annotation { "Feature Type Name" : "Feature", "Feature Type Description" : "" }
export const myFeature = defineFeature(function(context is Context, id is Id, definition is map)
    precondition{}
    {
        {
            var Q0;
            Q0=qCreatedBy(makeId("Front.planeOp"),FACE);
            var sketch = newSketch(context, id + "F0", { "sketchPlane" : qUnion([Q0])});
            skText(sketch, "E0", { "text": "Maya\'s Gymnastic Medals", "fontName": "OpenSans-Bold.ttf"});
            const initialGuessF0  = {"E0": [-0.0474, 0.00076, 1, 0, 0.0053]};
            skSetInitialGuess(sketch, initialGuessF0);
            skSolve(sketch);
        }
        {
            var Q0;
            Q0 = qSketchRegion(id + "F0", true);
            extrude(context, id + "F1", {"entities" : qUnion([Q0]), "depth" : 3 * mm, "offsetDistance" : 25 * mm});
        }
        {
            var Q0;
            Q0=makeQuery(id+"F1.opExtrude","SWEPT_BODY",BODY,{"disambiguationData":[OSD([sQuery(id+"F0.wireOp",EDGE,"E0.sketch_text.stroke-44"),sQuery(id+"F0.wireOp",EDGE,"E0.sketch_text.stroke-45"),sQuery(id+"F0.wireOp",EDGE,"E0.sketch_text.stroke-46"),sQuery(id+"F0.wireOp",EDGE,"E0.sketch_text.stroke-47"),sQuery(id+"F0.wireOp",EDGE,"E0.sketch_text.stroke-48"),sQuery(id+"F0.wireOp",EDGE,"E0.sketch_text.stroke-49"),sQuery(id+"F0.wireOp",EDGE,"E0.sketch_text.stroke-50"),sQuery(id+"F0.wireOp",EDGE,"E0.sketch_text.stroke-51"),sQuery(id+"F0.wireOp",EDGE,"E0.sketch_text.stroke-52"),sQuery(id+"F0.wireOp",EDGE,"E0.sketch_text.stroke-53"),sQuery(id+"F0.wireOp",EDGE,"E0.sketch_text.stroke-54"),sQuery(id+"F0.wireOp",EDGE,"E0.sketch_text.stroke-55"),sQuery(id+"F0.wireOp",EDGE,"E0.sketch_text.stroke-56"),sQuery(id+"F0.wireOp",EDGE,"E0.sketch_text.stroke-57"),sQuery(id+"F0.wireOp",EDGE,"E0.sketch_text.stroke-58"),sQuery(id+"F0.wireOp",EDGE,"E0.sketch_text.stroke-59"),sQuery(id+"F0.wireOp",EDGE,"E0.sketch_text.stroke-60")])]});
            var Q1;
            Q1=makeQuery(id+"F1.opExtrude","SWEPT_BODY",BODY,{"disambiguationData":[OSD([sQuery(id+"F0.wireOp",EDGE,"E0.sketch_text.stroke-135"),sQuery(id+"F0.wireOp",EDGE,"E0.sketch_text.stroke-136"),sQuery(id+"F0.wireOp",EDGE,"E0.sketch_text.stroke-137"),sQuery(id+"F0.wireOp",EDGE,"E0.sketch_text.stroke-138"),sQuery(id+"F0.wireOp",EDGE,"E0.sketch_text.stroke-139"),sQuery(id+"F0.wireOp",EDGE,"E0.sketch_text.stroke-140"),sQuery(id+"F0.wireOp",EDGE,"E0.sketch_text.stroke-141"),sQuery(id+"F0.wireOp",EDGE,"E0.sketch_text.stroke-142"),sQuery(id+"F0.wireOp",EDGE,"E0.sketch_text.stroke-143"),sQuery(id+"F0.wireOp",EDGE,"E0.sketch_text.stroke-144"),sQuery(id+"F0.wireOp",EDGE,"E0.sketch_text.stroke-145"),sQuery(id+"F0.wireOp",EDGE,"E0.sketch_text.stroke-146"),sQuery(id+"F0.wireOp",EDGE,"E0.sketch_text.stroke-147"),sQuery(id+"F0.wireOp",EDGE,"E0.sketch_text.stroke-148"),sQuery(id+"F0.wireOp",EDGE,"E0.sketch_text.stroke-149"),sQuery(id+"F0.wireOp",EDGE,"E0.sketch_text.stroke-150"),sQuery(id+"F0.wireOp",EDGE,"E0.sketch_text.stroke-151")])]});
            transform(context, id + "F2", {"entities" : qUnion([Q0, Q1]), "transformType" : TransformType.TRANSLATION_3D, "dx" : 0 * mm, "dy" : 0 * mm, "dz" : 1.5 * mm, "makeCopy" : false});
        }
        {
            var Q0;
            Q0=makeQuery(id+"F1.opExtrude","SWEPT_BODY",BODY,{"disambiguationData":[OSD([sQuery(id+"F0.wireOp",EDGE,"E0.sketch_text.stroke-86"),sQuery(id+"F0.wireOp",EDGE,"E0.sketch_text.stroke-87"),sQuery(id+"F0.wireOp",EDGE,"E0.sketch_text.stroke-88"),sQuery(id+"F0.wireOp",EDGE,"E0.sketch_text.stroke-89")])]});
            transform(context, id + "F3", {"entities" : qUnion([Q0]), "transformType" : TransformType.TRANSLATION_3D, "dx" : 1.25 * mm, "dy" : 0 * mm, "dz" : 0 * mm, "makeCopy" : false});
        }
        {
            var Q0;
            Q0=makeQuery(id+"F1.opExtrude","SWEPT_BODY",BODY,{"disambiguationData":[OSD([sQuery(id+"F0.wireOp",EDGE,"E0.sketch_text.stroke-90"),sQuery(id+"F0.wireOp",EDGE,"E0.sketch_text.stroke-91"),sQuery(id+"F0.wireOp",EDGE,"E0.sketch_text.stroke-92"),sQuery(id+"F0.wireOp",EDGE,"E0.sketch_text.stroke-93"),sQuery(id+"F0.wireOp",EDGE,"E0.sketch_text.stroke-94"),sQuery(id+"F0.wireOp",EDGE,"E0.sketch_text.stroke-95"),sQuery(id+"F0.wireOp",EDGE,"E0.sketch_text.stroke-96"),sQuery(id+"F0.wireOp",EDGE,"E0.sketch_text.stroke-97"),sQuery(id+"F0.wireOp",EDGE,"E0.sketch_text.stroke-98"),sQuery(id+"F0.wireOp",EDGE,"E0.sketch_text.stroke-99"),sQuery(id+"F0.wireOp",EDGE,"E0.sketch_text.stroke-100"),sQuery(id+"F0.wireOp",EDGE,"E0.sketch_text.stroke-101"),sQuery(id+"F0.wireOp",EDGE,"E0.sketch_text.stroke-102"),sQuery(id+"F0.wireOp",EDGE,"E0.sketch_text.stroke-103"),sQuery(id+"F0.wireOp",EDGE,"E0.sketch_text.stroke-104"),sQuery(id+"F0.wireOp",EDGE,"E0.sketch_text.stroke-105"),sQuery(id+"F0.wireOp",EDGE,"E0.sketch_text.stroke-106"),sQuery(id+"F0.wireOp",EDGE,"E0.sketch_text.stroke-107"),sQuery(id+"F0.wireOp",EDGE,"E0.sketch_text.stroke-108"),sQuery(id+"F0.wireOp",EDGE,"E0.sketch_text.stroke-109"),sQuery(id+"F0.wireOp",EDGE,"E0.sketch_text.stroke-110"),sQuery(id+"F0.wireOp",EDGE,"E0.sketch_text.stroke-111"),sQuery(id+"F0.wireOp",EDGE,"E0.sketch_text.stroke-112"),sQuery(id+"F0.wireOp",EDGE,"E0.sketch_text.stroke-113"),sQuery(id+"F0.wireOp",EDGE,"E0.sketch_text.stroke-114"),sQuery(id+"F0.wireOp",EDGE,"E0.sketch_text.stroke-115")])]});
            var Q1;
            Q1=makeQuery(id+"F1.opExtrude","SWEPT_BODY",BODY,{"disambiguationData":[OSD([sQuery(id+"F0.wireOp",EDGE,"E0.sketch_text.stroke-86"),sQuery(id+"F0.wireOp",EDGE,"E0.sketch_text.stroke-87"),sQuery(id+"F0.wireOp",EDGE,"E0.sketch_text.stroke-88"),sQuery(id+"F0.wireOp",EDGE,"E0.sketch_text.stroke-89")])]});
            transform(context, id + "F4", {"entities" : qUnion([Q0, Q1]), "transformType" : TransformType.TRANSLATION_3D, "dx" : -1.52 * mm, "dy" : 0 * mm, "dz" : 0.16 * mm, "makeCopy" : false});
        }
        {
            var Q0;
            Q0=makeQuery(id+"F1.opExtrude","SWEPT_BODY",BODY,{"disambiguationData":[OSD([sQuery(id+"F0.wireOp",EDGE,"E0.sketch_text.stroke-135"),sQuery(id+"F0.wireOp",EDGE,"E0.sketch_text.stroke-136"),sQuery(id+"F0.wireOp",EDGE,"E0.sketch_text.stroke-137"),sQuery(id+"F0.wireOp",EDGE,"E0.sketch_text.stroke-138"),sQuery(id+"F0.wireOp",EDGE,"E0.sketch_text.stroke-139"),sQuery(id+"F0.wireOp",EDGE,"E0.sketch_text.stroke-140"),sQuery(id+"F0.wireOp",EDGE,"E0.sketch_text.stroke-141"),sQuery(id+"F0.wireOp",EDGE,"E0.sketch_text.stroke-142"),sQuery(id+"F0.wireOp",EDGE,"E0.sketch_text.stroke-143"),sQuery(id+"F0.wireOp",EDGE,"E0.sketch_text.stroke-144"),sQuery(id+"F0.wireOp",EDGE,"E0.sketch_text.stroke-145"),sQuery(id+"F0.wireOp",EDGE,"E0.sketch_text.stroke-146"),sQuery(id+"F0.wireOp",EDGE,"E0.sketch_text.stroke-147"),sQuery(id+"F0.wireOp",EDGE,"E0.sketch_text.stroke-148"),sQuery(id+"F0.wireOp",EDGE,"E0.sketch_text.stroke-149"),sQuery(id+"F0.wireOp",EDGE,"E0.sketch_text.stroke-150"),sQuery(id+"F0.wireOp",EDGE,"E0.sketch_text.stroke-151")])]});
            var Q1;
            Q1=makeQuery(id+"F1.opExtrude","SWEPT_BODY",BODY,{"disambiguationData":[OSD([sQuery(id+"F0.wireOp",EDGE,"E0.sketch_text.stroke-44"),sQuery(id+"F0.wireOp",EDGE,"E0.sketch_text.stroke-45"),sQuery(id+"F0.wireOp",EDGE,"E0.sketch_text.stroke-46"),sQuery(id+"F0.wireOp",EDGE,"E0.sketch_text.stroke-47"),sQuery(id+"F0.wireOp",EDGE,"E0.sketch_text.stroke-48"),sQuery(id+"F0.wireOp",EDGE,"E0.sketch_text.stroke-49"),sQuery(id+"F0.wireOp",EDGE,"E0.sketch_text.stroke-50"),sQuery(id+"F0.wireOp",EDGE,"E0.sketch_text.stroke-51"),sQuery(id+"F0.wireOp",EDGE,"E0.sketch_text.stroke-52"),sQuery(id+"F0.wireOp",EDGE,"E0.sketch_text.stroke-53"),sQuery(id+"F0.wireOp",EDGE,"E0.sketch_text.stroke-54"),sQuery(id+"F0.wireOp",EDGE,"E0.sketch_text.stroke-55"),sQuery(id+"F0.wireOp",EDGE,"E0.sketch_text.stroke-56"),sQuery(id+"F0.wireOp",EDGE,"E0.sketch_text.stroke-57"),sQuery(id+"F0.wireOp",EDGE,"E0.sketch_text.stroke-58"),sQuery(id+"F0.wireOp",EDGE,"E0.sketch_text.stroke-59"),sQuery(id+"F0.wireOp",EDGE,"E0.sketch_text.stroke-60")])]});
            transform(context, id + "F5", {"entities" : qUnion([Q0, Q1]), "transformType" : TransformType.TRANSLATION_3D, "dx" : 0 * mm, "dy" : 0 * mm, "dz" : -0.7 * mm, "makeCopy" : false});
        }
        {
            var Q0;
            Q0=makeQuery(id+"F1.opExtrude","SWEPT_BODY",BODY,{"disambiguationData":[OSD([sQuery(id+"F0.wireOp",EDGE,"E0.sketch_text.stroke-266"),sQuery(id+"F0.wireOp",EDGE,"E0.sketch_text.stroke-267"),sQuery(id+"F0.wireOp",EDGE,"E0.sketch_text.stroke-268"),sQuery(id+"F0.wireOp",EDGE,"E0.sketch_text.stroke-269"),sQuery(id+"F0.wireOp",EDGE,"E0.sketch_text.stroke-270")])]});
            transform(context, id + "F6", {"entities" : qUnion([Q0]), "transformType" : TransformType.TRANSLATION_3D, "dx" : 0 * mm, "dy" : 0 * mm, "dz" : -0.5 * mm, "makeCopy" : false});
        }
        {
            var Q0;
            Q0=qCreatedBy(makeId("Front.planeOp"),FACE);
            var sketch = newSketch(context, id + "F7", { "sketchPlane" : qUnion([Q0])});
            skLineSegment(sketch, "E1.bottom", {"start": v(-47.66, 1.2) * mm, "end": v(49.34, 1.2) * mm});
            skLineSegment(sketch, "E1.top", {"start": v(-47.66, 0) * mm, "end": v(49.34, 0) * mm});
            skLineSegment(sketch, "E1.left", {"start": v(-47.66, 1.2) * mm, "end": v(-47.66, 0) * mm});
            skLineSegment(sketch, "E1.right", {"start": v(49.34, 1.2) * mm, "end": v(49.34, 0) * mm});
            skSolve(sketch);
        }
        {
            var Q0;
            Q0 = qSketchRegion(id + "F7", true);
            extrude(context, id + "F8", {"entities" : qUnion([Q0]), "depth" : 3.5 * mm, "offsetDistance" : 25 * mm});
        }
        {
            var Q0;
            Q0=makeQuery(id+"F8.opExtrude","SWEPT_BODY",BODY,{"disambiguationData":[OSD([sQuery(id+"F7.wireOp",EDGE,"E1.bottom"),sQuery(id+"F7.wireOp",EDGE,"E1.top"),sQuery(id+"F7.wireOp",EDGE,"E1.left"),sQuery(id+"F7.wireOp",EDGE,"E1.right")])]});
            transform(context, id + "F9", {"entities" : qUnion([Q0]), "transformType" : TransformType.TRANSLATION_3D, "dx" : 0 * mm, "dy" : 0 * mm, "dz" : -.3 * mm, "makeCopy" : false});
        }
        {
            var Q0;
            Q0=qCreatedBy(makeId("Front.planeOp"),FACE);
            var sketch = newSketch(context, id + "F10", { "sketchPlane" : qUnion([Q0])});
            skText(sketch, "E2", { "text": "Claddagh School Of Irish Dancing", "fontName": "OpenSans-Bold.ttf"});
            const initialGuessF10  = {"E2": [-0.01998, -0.01626, 1, 0, 0.00568]};
            skSetInitialGuess(sketch, initialGuessF10);
            skSolve(sketch);
        }
        {
            var Q0;
            Q0 = qSketchRegion(id + "F10", true);
            extrude(context, id + "F11", {"entities" : qUnion([Q0]), "depth" : 3.5 * mm, "offsetDistance" : 25 * mm});
        }
        {
            var Q0;
            Q0=makeQuery(id+"F11.opExtrude","SWEPT_BODY",BODY,{"disambiguationData":[OSD([sQuery(id+"F10.wireOp",EDGE,"E2.sketch_text.stroke-0"),sQuery(id+"F10.wireOp",EDGE,"E2.sketch_text.stroke-1"),sQuery(id+"F10.wireOp",EDGE,"E2.sketch_text.stroke-2"),sQuery(id+"F10.wireOp",EDGE,"E2.sketch_text.stroke-3"),sQuery(id+"F10.wireOp",EDGE,"E2.sketch_text.stroke-4"),sQuery(id+"F10.wireOp",EDGE,"E2.sketch_text.stroke-5"),sQuery(id+"F10.wireOp",EDGE,"E2.sketch_text.stroke-6"),sQuery(id+"F10.wireOp",EDGE,"E2.sketch_text.stroke-7"),sQuery(id+"F10.wireOp",EDGE,"E2.sketch_text.stroke-8"),sQuery(id+"F10.wireOp",EDGE,"E2.sketch_text.stroke-9"),sQuery(id+"F10.wireOp",EDGE,"E2.sketch_text.stroke-10"),sQuery(id+"F10.wireOp",EDGE,"E2.sketch_text.stroke-11"),sQuery(id+"F10.wireOp",EDGE,"E2.sketch_text.stroke-12"),sQuery(id+"F10.wireOp",EDGE,"E2.sketch_text.stroke-13"),sQuery(id+"F10.wireOp",EDGE,"E2.sketch_text.stroke-14")])]});
            var Q1;
            Q1=makeQuery(id+"F11.opExtrude","SWEPT_BODY",BODY,{"disambiguationData":[OSD([sQuery(id+"F10.wireOp",EDGE,"E2.sketch_text.stroke-15"),sQuery(id+"F10.wireOp",EDGE,"E2.sketch_text.stroke-16"),sQuery(id+"F10.wireOp",EDGE,"E2.sketch_text.stroke-17"),sQuery(id+"F10.wireOp",EDGE,"E2.sketch_text.stroke-18")])]});
            var Q2;
            Q2=makeQuery(id+"F11.opExtrude","SWEPT_BODY",BODY,{"disambiguationData":[OSD([sQuery(id+"F10.wireOp",EDGE,"E2.sketch_text.stroke-19"),sQuery(id+"F10.wireOp",EDGE,"E2.sketch_text.stroke-20"),sQuery(id+"F10.wireOp",EDGE,"E2.sketch_text.stroke-21"),sQuery(id+"F10.wireOp",EDGE,"E2.sketch_text.stroke-22"),sQuery(id+"F10.wireOp",EDGE,"E2.sketch_text.stroke-23"),sQuery(id+"F10.wireOp",EDGE,"E2.sketch_text.stroke-24"),sQuery(id+"F10.wireOp",EDGE,"E2.sketch_text.stroke-25"),sQuery(id+"F10.wireOp",EDGE,"E2.sketch_text.stroke-26"),sQuery(id+"F10.wireOp",EDGE,"E2.sketch_text.stroke-27"),sQuery(id+"F10.wireOp",EDGE,"E2.sketch_text.stroke-28"),sQuery(id+"F10.wireOp",EDGE,"E2.sketch_text.stroke-29"),sQuery(id+"F10.wireOp",EDGE,"E2.sketch_text.stroke-30"),sQuery(id+"F10.wireOp",EDGE,"E2.sketch_text.stroke-31"),sQuery(id+"F10.wireOp",EDGE,"E2.sketch_text.stroke-32"),sQuery(id+"F10.wireOp",EDGE,"E2.sketch_text.stroke-33"),sQuery(id+"F10.wireOp",EDGE,"E2.sketch_text.stroke-34"),sQuery(id+"F10.wireOp",EDGE,"E2.sketch_text.stroke-35"),sQuery(id+"F10.wireOp",EDGE,"E2.sketch_text.stroke-36"),sQuery(id+"F10.wireOp",EDGE,"E2.sketch_text.stroke-37"),sQuery(id+"F10.wireOp",EDGE,"E2.sketch_text.stroke-38"),sQuery(id+"F10.wireOp",EDGE,"E2.sketch_text.stroke-39"),sQuery(id+"F10.wireOp",EDGE,"E2.sketch_text.stroke-40"),sQuery(id+"F10.wireOp",EDGE,"E2.sketch_text.stroke-41"),sQuery(id+"F10.wireOp",EDGE,"E2.sketch_text.stroke-42"),sQuery(id+"F10.wireOp",EDGE,"E2.sketch_text.stroke-43")])]});
            var Q3;
            Q3=makeQuery(id+"F11.opExtrude","SWEPT_BODY",BODY,{"disambiguationData":[OSD([sQuery(id+"F10.wireOp",EDGE,"E2.sketch_text.stroke-44"),sQuery(id+"F10.wireOp",EDGE,"E2.sketch_text.stroke-45"),sQuery(id+"F10.wireOp",EDGE,"E2.sketch_text.stroke-46"),sQuery(id+"F10.wireOp",EDGE,"E2.sketch_text.stroke-47"),sQuery(id+"F10.wireOp",EDGE,"E2.sketch_text.stroke-48"),sQuery(id+"F10.wireOp",EDGE,"E2.sketch_text.stroke-49"),sQuery(id+"F10.wireOp",EDGE,"E2.sketch_text.stroke-50"),sQuery(id+"F10.wireOp",EDGE,"E2.sketch_text.stroke-51"),sQuery(id+"F10.wireOp",EDGE,"E2.sketch_text.stroke-52"),sQuery(id+"F10.wireOp",EDGE,"E2.sketch_text.stroke-53"),sQuery(id+"F10.wireOp",EDGE,"E2.sketch_text.stroke-54"),sQuery(id+"F10.wireOp",EDGE,"E2.sketch_text.stroke-55"),sQuery(id+"F10.wireOp",EDGE,"E2.sketch_text.stroke-56"),sQuery(id+"F10.wireOp",EDGE,"E2.sketch_text.stroke-57"),sQuery(id+"F10.wireOp",EDGE,"E2.sketch_text.stroke-58"),sQuery(id+"F10.wireOp",EDGE,"E2.sketch_text.stroke-59"),sQuery(id+"F10.wireOp",EDGE,"E2.sketch_text.stroke-60"),sQuery(id+"F10.wireOp",EDGE,"E2.sketch_text.stroke-61"),sQuery(id+"F10.wireOp",EDGE,"E2.sketch_text.stroke-62"),sQuery(id+"F10.wireOp",EDGE,"E2.sketch_text.stroke-63"),sQuery(id+"F10.wireOp",EDGE,"E2.sketch_text.stroke-64"),sQuery(id+"F10.wireOp",EDGE,"E2.sketch_text.stroke-65"),sQuery(id+"F10.wireOp",EDGE,"E2.sketch_text.stroke-66")])]});
            var Q4;
            Q4=makeQuery(id+"F11.opExtrude","SWEPT_BODY",BODY,{"disambiguationData":[OSD([sQuery(id+"F10.wireOp",EDGE,"E2.sketch_text.stroke-67"),sQuery(id+"F10.wireOp",EDGE,"E2.sketch_text.stroke-68"),sQuery(id+"F10.wireOp",EDGE,"E2.sketch_text.stroke-69"),sQuery(id+"F10.wireOp",EDGE,"E2.sketch_text.stroke-70"),sQuery(id+"F10.wireOp",EDGE,"E2.sketch_text.stroke-71"),sQuery(id+"F10.wireOp",EDGE,"E2.sketch_text.stroke-72"),sQuery(id+"F10.wireOp",EDGE,"E2.sketch_text.stroke-73"),sQuery(id+"F10.wireOp",EDGE,"E2.sketch_text.stroke-74"),sQuery(id+"F10.wireOp",EDGE,"E2.sketch_text.stroke-75"),sQuery(id+"F10.wireOp",EDGE,"E2.sketch_text.stroke-76"),sQuery(id+"F10.wireOp",EDGE,"E2.sketch_text.stroke-77"),sQuery(id+"F10.wireOp",EDGE,"E2.sketch_text.stroke-78"),sQuery(id+"F10.wireOp",EDGE,"E2.sketch_text.stroke-79"),sQuery(id+"F10.wireOp",EDGE,"E2.sketch_text.stroke-80"),sQuery(id+"F10.wireOp",EDGE,"E2.sketch_text.stroke-81"),sQuery(id+"F10.wireOp",EDGE,"E2.sketch_text.stroke-82"),sQuery(id+"F10.wireOp",EDGE,"E2.sketch_text.stroke-83"),sQuery(id+"F10.wireOp",EDGE,"E2.sketch_text.stroke-84"),sQuery(id+"F10.wireOp",EDGE,"E2.sketch_text.stroke-85"),sQuery(id+"F10.wireOp",EDGE,"E2.sketch_text.stroke-86"),sQuery(id+"F10.wireOp",EDGE,"E2.sketch_text.stroke-87"),sQuery(id+"F10.wireOp",EDGE,"E2.sketch_text.stroke-88"),sQuery(id+"F10.wireOp",EDGE,"E2.sketch_text.stroke-89")])]});
            var Q5;
            Q5=makeQuery(id+"F11.opExtrude","SWEPT_BODY",BODY,{"disambiguationData":[OSD([sQuery(id+"F10.wireOp",EDGE,"E2.sketch_text.stroke-90"),sQuery(id+"F10.wireOp",EDGE,"E2.sketch_text.stroke-91"),sQuery(id+"F10.wireOp",EDGE,"E2.sketch_text.stroke-92"),sQuery(id+"F10.wireOp",EDGE,"E2.sketch_text.stroke-93"),sQuery(id+"F10.wireOp",EDGE,"E2.sketch_text.stroke-94"),sQuery(id+"F10.wireOp",EDGE,"E2.sketch_text.stroke-95"),sQuery(id+"F10.wireOp",EDGE,"E2.sketch_text.stroke-96"),sQuery(id+"F10.wireOp",EDGE,"E2.sketch_text.stroke-97"),sQuery(id+"F10.wireOp",EDGE,"E2.sketch_text.stroke-98"),sQuery(id+"F10.wireOp",EDGE,"E2.sketch_text.stroke-99"),sQuery(id+"F10.wireOp",EDGE,"E2.sketch_text.stroke-100"),sQuery(id+"F10.wireOp",EDGE,"E2.sketch_text.stroke-101"),sQuery(id+"F10.wireOp",EDGE,"E2.sketch_text.stroke-102"),sQuery(id+"F10.wireOp",EDGE,"E2.sketch_text.stroke-103"),sQuery(id+"F10.wireOp",EDGE,"E2.sketch_text.stroke-104"),sQuery(id+"F10.wireOp",EDGE,"E2.sketch_text.stroke-105"),sQuery(id+"F10.wireOp",EDGE,"E2.sketch_text.stroke-106"),sQuery(id+"F10.wireOp",EDGE,"E2.sketch_text.stroke-107"),sQuery(id+"F10.wireOp",EDGE,"E2.sketch_text.stroke-108"),sQuery(id+"F10.wireOp",EDGE,"E2.sketch_text.stroke-109"),sQuery(id+"F10.wireOp",EDGE,"E2.sketch_text.stroke-110"),sQuery(id+"F10.wireOp",EDGE,"E2.sketch_text.stroke-111"),sQuery(id+"F10.wireOp",EDGE,"E2.sketch_text.stroke-112"),sQuery(id+"F10.wireOp",EDGE,"E2.sketch_text.stroke-113"),sQuery(id+"F10.wireOp",EDGE,"E2.sketch_text.stroke-114")])]});
            var Q6;
            Q6=makeQuery(id+"F11.opExtrude","SWEPT_BODY",BODY,{"disambiguationData":[OSD([sQuery(id+"F10.wireOp",EDGE,"E2.sketch_text.stroke-115"),sQuery(id+"F10.wireOp",EDGE,"E2.sketch_text.stroke-116"),sQuery(id+"F10.wireOp",EDGE,"E2.sketch_text.stroke-117"),sQuery(id+"F10.wireOp",EDGE,"E2.sketch_text.stroke-118"),sQuery(id+"F10.wireOp",EDGE,"E2.sketch_text.stroke-119"),sQuery(id+"F10.wireOp",EDGE,"E2.sketch_text.stroke-120"),sQuery(id+"F10.wireOp",EDGE,"E2.sketch_text.stroke-121"),sQuery(id+"F10.wireOp",EDGE,"E2.sketch_text.stroke-122"),sQuery(id+"F10.wireOp",EDGE,"E2.sketch_text.stroke-123"),sQuery(id+"F10.wireOp",EDGE,"E2.sketch_text.stroke-124"),sQuery(id+"F10.wireOp",EDGE,"E2.sketch_text.stroke-125"),sQuery(id+"F10.wireOp",EDGE,"E2.sketch_text.stroke-126"),sQuery(id+"F10.wireOp",EDGE,"E2.sketch_text.stroke-127"),sQuery(id+"F10.wireOp",EDGE,"E2.sketch_text.stroke-128"),sQuery(id+"F10.wireOp",EDGE,"E2.sketch_text.stroke-129"),sQuery(id+"F10.wireOp",EDGE,"E2.sketch_text.stroke-130"),sQuery(id+"F10.wireOp",EDGE,"E2.sketch_text.stroke-131"),sQuery(id+"F10.wireOp",EDGE,"E2.sketch_text.stroke-132"),sQuery(id+"F10.wireOp",EDGE,"E2.sketch_text.stroke-133"),sQuery(id+"F10.wireOp",EDGE,"E2.sketch_text.stroke-134"),sQuery(id+"F10.wireOp",EDGE,"E2.sketch_text.stroke-135"),sQuery(id+"F10.wireOp",EDGE,"E2.sketch_text.stroke-136"),sQuery(id+"F10.wireOp",EDGE,"E2.sketch_text.stroke-137"),sQuery(id+"F10.wireOp",EDGE,"E2.sketch_text.stroke-138"),sQuery(id+"F10.wireOp",EDGE,"E2.sketch_text.stroke-139"),sQuery(id+"F10.wireOp",EDGE,"E2.sketch_text.stroke-140"),sQuery(id+"F10.wireOp",EDGE,"E2.sketch_text.stroke-141"),sQuery(id+"F10.wireOp",EDGE,"E2.sketch_text.stroke-142"),sQuery(id+"F10.wireOp",EDGE,"E2.sketch_text.stroke-143"),sQuery(id+"F10.wireOp",EDGE,"E2.sketch_text.stroke-144"),sQuery(id+"F10.wireOp",EDGE,"E2.sketch_text.stroke-145"),sQuery(id+"F10.wireOp",EDGE,"E2.sketch_text.stroke-146"),sQuery(id+"F10.wireOp",EDGE,"E2.sketch_text.stroke-147"),sQuery(id+"F10.wireOp",EDGE,"E2.sketch_text.stroke-148"),sQuery(id+"F10.wireOp",EDGE,"E2.sketch_text.stroke-149"),sQuery(id+"F10.wireOp",EDGE,"E2.sketch_text.stroke-150"),sQuery(id+"F10.wireOp",EDGE,"E2.sketch_text.stroke-151"),sQuery(id+"F10.wireOp",EDGE,"E2.sketch_text.stroke-152"),sQuery(id+"F10.wireOp",EDGE,"E2.sketch_text.stroke-153"),sQuery(id+"F10.wireOp",EDGE,"E2.sketch_text.stroke-154"),sQuery(id+"F10.wireOp",EDGE,"E2.sketch_text.stroke-155"),sQuery(id+"F10.wireOp",EDGE,"E2.sketch_text.stroke-156"),sQuery(id+"F10.wireOp",EDGE,"E2.sketch_text.stroke-157"),sQuery(id+"F10.wireOp",EDGE,"E2.sketch_text.stroke-158")])]});
            var Q7;
            Q7=makeQuery(id+"F11.opExtrude","SWEPT_BODY",BODY,{"disambiguationData":[OSD([sQuery(id+"F10.wireOp",EDGE,"E2.sketch_text.stroke-159"),sQuery(id+"F10.wireOp",EDGE,"E2.sketch_text.stroke-160"),sQuery(id+"F10.wireOp",EDGE,"E2.sketch_text.stroke-161"),sQuery(id+"F10.wireOp",EDGE,"E2.sketch_text.stroke-162"),sQuery(id+"F10.wireOp",EDGE,"E2.sketch_text.stroke-163"),sQuery(id+"F10.wireOp",EDGE,"E2.sketch_text.stroke-164"),sQuery(id+"F10.wireOp",EDGE,"E2.sketch_text.stroke-165"),sQuery(id+"F10.wireOp",EDGE,"E2.sketch_text.stroke-166"),sQuery(id+"F10.wireOp",EDGE,"E2.sketch_text.stroke-167"),sQuery(id+"F10.wireOp",EDGE,"E2.sketch_text.stroke-168"),sQuery(id+"F10.wireOp",EDGE,"E2.sketch_text.stroke-169"),sQuery(id+"F10.wireOp",EDGE,"E2.sketch_text.stroke-170"),sQuery(id+"F10.wireOp",EDGE,"E2.sketch_text.stroke-171"),sQuery(id+"F10.wireOp",EDGE,"E2.sketch_text.stroke-172"),sQuery(id+"F10.wireOp",EDGE,"E2.sketch_text.stroke-173"),sQuery(id+"F10.wireOp",EDGE,"E2.sketch_text.stroke-174"),sQuery(id+"F10.wireOp",EDGE,"E2.sketch_text.stroke-175")])]});
            var Q8;
            Q8=makeQuery(id+"F11.opExtrude","SWEPT_BODY",BODY,{"disambiguationData":[OSD([sQuery(id+"F10.wireOp",EDGE,"E2.sketch_text.stroke-176"),sQuery(id+"F10.wireOp",EDGE,"E2.sketch_text.stroke-177"),sQuery(id+"F10.wireOp",EDGE,"E2.sketch_text.stroke-178"),sQuery(id+"F10.wireOp",EDGE,"E2.sketch_text.stroke-179"),sQuery(id+"F10.wireOp",EDGE,"E2.sketch_text.stroke-180"),sQuery(id+"F10.wireOp",EDGE,"E2.sketch_text.stroke-181"),sQuery(id+"F10.wireOp",EDGE,"E2.sketch_text.stroke-182"),sQuery(id+"F10.wireOp",EDGE,"E2.sketch_text.stroke-183"),sQuery(id+"F10.wireOp",EDGE,"E2.sketch_text.stroke-184"),sQuery(id+"F10.wireOp",EDGE,"E2.sketch_text.stroke-185"),sQuery(id+"F10.wireOp",EDGE,"E2.sketch_text.stroke-186"),sQuery(id+"F10.wireOp",EDGE,"E2.sketch_text.stroke-187"),sQuery(id+"F10.wireOp",EDGE,"E2.sketch_text.stroke-188"),sQuery(id+"F10.wireOp",EDGE,"E2.sketch_text.stroke-189"),sQuery(id+"F10.wireOp",EDGE,"E2.sketch_text.stroke-190"),sQuery(id+"F10.wireOp",EDGE,"E2.sketch_text.stroke-191"),sQuery(id+"F10.wireOp",EDGE,"E2.sketch_text.stroke-192"),sQuery(id+"F10.wireOp",EDGE,"E2.sketch_text.stroke-193"),sQuery(id+"F10.wireOp",EDGE,"E2.sketch_text.stroke-194"),sQuery(id+"F10.wireOp",EDGE,"E2.sketch_text.stroke-195"),sQuery(id+"F10.wireOp",EDGE,"E2.sketch_text.stroke-196"),sQuery(id+"F10.wireOp",EDGE,"E2.sketch_text.stroke-197"),sQuery(id+"F10.wireOp",EDGE,"E2.sketch_text.stroke-198"),sQuery(id+"F10.wireOp",EDGE,"E2.sketch_text.stroke-199"),sQuery(id+"F10.wireOp",EDGE,"E2.sketch_text.stroke-200"),sQuery(id+"F10.wireOp",EDGE,"E2.sketch_text.stroke-201"),sQuery(id+"F10.wireOp",EDGE,"E2.sketch_text.stroke-202"),sQuery(id+"F10.wireOp",EDGE,"E2.sketch_text.stroke-203")])]});
            var Q9;
            Q9=makeQuery(id+"F11.opExtrude","SWEPT_BODY",BODY,{"disambiguationData":[OSD([sQuery(id+"F10.wireOp",EDGE,"E2.sketch_text.stroke-204"),sQuery(id+"F10.wireOp",EDGE,"E2.sketch_text.stroke-205"),sQuery(id+"F10.wireOp",EDGE,"E2.sketch_text.stroke-206"),sQuery(id+"F10.wireOp",EDGE,"E2.sketch_text.stroke-207"),sQuery(id+"F10.wireOp",EDGE,"E2.sketch_text.stroke-208"),sQuery(id+"F10.wireOp",EDGE,"E2.sketch_text.stroke-209"),sQuery(id+"F10.wireOp",EDGE,"E2.sketch_text.stroke-210"),sQuery(id+"F10.wireOp",EDGE,"E2.sketch_text.stroke-211"),sQuery(id+"F10.wireOp",EDGE,"E2.sketch_text.stroke-212"),sQuery(id+"F10.wireOp",EDGE,"E2.sketch_text.stroke-213"),sQuery(id+"F10.wireOp",EDGE,"E2.sketch_text.stroke-214"),sQuery(id+"F10.wireOp",EDGE,"E2.sketch_text.stroke-215"),sQuery(id+"F10.wireOp",EDGE,"E2.sketch_text.stroke-216"),sQuery(id+"F10.wireOp",EDGE,"E2.sketch_text.stroke-217")])]});
            var Q10;
            Q10=makeQuery(id+"F11.opExtrude","SWEPT_BODY",BODY,{"disambiguationData":[OSD([sQuery(id+"F10.wireOp",EDGE,"E2.sketch_text.stroke-218"),sQuery(id+"F10.wireOp",EDGE,"E2.sketch_text.stroke-219"),sQuery(id+"F10.wireOp",EDGE,"E2.sketch_text.stroke-220"),sQuery(id+"F10.wireOp",EDGE,"E2.sketch_text.stroke-221"),sQuery(id+"F10.wireOp",EDGE,"E2.sketch_text.stroke-222"),sQuery(id+"F10.wireOp",EDGE,"E2.sketch_text.stroke-223"),sQuery(id+"F10.wireOp",EDGE,"E2.sketch_text.stroke-224"),sQuery(id+"F10.wireOp",EDGE,"E2.sketch_text.stroke-225"),sQuery(id+"F10.wireOp",EDGE,"E2.sketch_text.stroke-226"),sQuery(id+"F10.wireOp",EDGE,"E2.sketch_text.stroke-227"),sQuery(id+"F10.wireOp",EDGE,"E2.sketch_text.stroke-228"),sQuery(id+"F10.wireOp",EDGE,"E2.sketch_text.stroke-229"),sQuery(id+"F10.wireOp",EDGE,"E2.sketch_text.stroke-230"),sQuery(id+"F10.wireOp",EDGE,"E2.sketch_text.stroke-231"),sQuery(id+"F10.wireOp",EDGE,"E2.sketch_text.stroke-232"),sQuery(id+"F10.wireOp",EDGE,"E2.sketch_text.stroke-233"),sQuery(id+"F10.wireOp",EDGE,"E2.sketch_text.stroke-234")])]});
            var Q11;
            Q11=makeQuery(id+"F11.opExtrude","SWEPT_BODY",BODY,{"disambiguationData":[OSD([sQuery(id+"F10.wireOp",EDGE,"E2.sketch_text.stroke-235"),sQuery(id+"F10.wireOp",EDGE,"E2.sketch_text.stroke-236"),sQuery(id+"F10.wireOp",EDGE,"E2.sketch_text.stroke-237"),sQuery(id+"F10.wireOp",EDGE,"E2.sketch_text.stroke-238"),sQuery(id+"F10.wireOp",EDGE,"E2.sketch_text.stroke-239"),sQuery(id+"F10.wireOp",EDGE,"E2.sketch_text.stroke-240"),sQuery(id+"F10.wireOp",EDGE,"E2.sketch_text.stroke-241"),sQuery(id+"F10.wireOp",EDGE,"E2.sketch_text.stroke-242"),sQuery(id+"F10.wireOp",EDGE,"E2.sketch_text.stroke-243"),sQuery(id+"F10.wireOp",EDGE,"E2.sketch_text.stroke-244"),sQuery(id+"F10.wireOp",EDGE,"E2.sketch_text.stroke-245"),sQuery(id+"F10.wireOp",EDGE,"E2.sketch_text.stroke-246"),sQuery(id+"F10.wireOp",EDGE,"E2.sketch_text.stroke-247"),sQuery(id+"F10.wireOp",EDGE,"E2.sketch_text.stroke-248"),sQuery(id+"F10.wireOp",EDGE,"E2.sketch_text.stroke-249"),sQuery(id+"F10.wireOp",EDGE,"E2.sketch_text.stroke-250"),sQuery(id+"F10.wireOp",EDGE,"E2.sketch_text.stroke-251"),sQuery(id+"F10.wireOp",EDGE,"E2.sketch_text.stroke-252")])]});
            var Q12;
            Q12=makeQuery(id+"F11.opExtrude","SWEPT_BODY",BODY,{"disambiguationData":[OSD([sQuery(id+"F10.wireOp",EDGE,"E2.sketch_text.stroke-253"),sQuery(id+"F10.wireOp",EDGE,"E2.sketch_text.stroke-254"),sQuery(id+"F10.wireOp",EDGE,"E2.sketch_text.stroke-255"),sQuery(id+"F10.wireOp",EDGE,"E2.sketch_text.stroke-256"),sQuery(id+"F10.wireOp",EDGE,"E2.sketch_text.stroke-257"),sQuery(id+"F10.wireOp",EDGE,"E2.sketch_text.stroke-258"),sQuery(id+"F10.wireOp",EDGE,"E2.sketch_text.stroke-259"),sQuery(id+"F10.wireOp",EDGE,"E2.sketch_text.stroke-260"),sQuery(id+"F10.wireOp",EDGE,"E2.sketch_text.stroke-261"),sQuery(id+"F10.wireOp",EDGE,"E2.sketch_text.stroke-262"),sQuery(id+"F10.wireOp",EDGE,"E2.sketch_text.stroke-263"),sQuery(id+"F10.wireOp",EDGE,"E2.sketch_text.stroke-264"),sQuery(id+"F10.wireOp",EDGE,"E2.sketch_text.stroke-265"),sQuery(id+"F10.wireOp",EDGE,"E2.sketch_text.stroke-266"),sQuery(id+"F10.wireOp",EDGE,"E2.sketch_text.stroke-267"),sQuery(id+"F10.wireOp",EDGE,"E2.sketch_text.stroke-268"),sQuery(id+"F10.wireOp",EDGE,"E2.sketch_text.stroke-269"),sQuery(id+"F10.wireOp",EDGE,"E2.sketch_text.stroke-270")])]});
            var Q13;
            Q13=makeQuery(id+"F11.opExtrude","SWEPT_BODY",BODY,{"disambiguationData":[OSD([sQuery(id+"F10.wireOp",EDGE,"E2.sketch_text.stroke-271"),sQuery(id+"F10.wireOp",EDGE,"E2.sketch_text.stroke-272"),sQuery(id+"F10.wireOp",EDGE,"E2.sketch_text.stroke-273"),sQuery(id+"F10.wireOp",EDGE,"E2.sketch_text.stroke-274")])]});
            transform(context, id + "F12", {"entities" : qUnion([Q0, Q1, Q2, Q3, Q4, Q5, Q6, Q7, Q8, Q9, Q10, Q11, Q12, Q13]), "transformType" : TransformType.TRANSLATION_3D, "dx" : 65.6 * mm, "dy" : 0 * mm, "dz" : 7.1 * mm, "makeCopy" : false});
        }
        {
            var Q0;
            Q0=makeQuery(id+"F11.opExtrude","SWEPT_BODY",BODY,{"disambiguationData":[OSD([sQuery(id+"F10.wireOp",EDGE,"E2.sketch_text.stroke-115"),sQuery(id+"F10.wireOp",EDGE,"E2.sketch_text.stroke-116"),sQuery(id+"F10.wireOp",EDGE,"E2.sketch_text.stroke-117"),sQuery(id+"F10.wireOp",EDGE,"E2.sketch_text.stroke-118"),sQuery(id+"F10.wireOp",EDGE,"E2.sketch_text.stroke-119"),sQuery(id+"F10.wireOp",EDGE,"E2.sketch_text.stroke-120"),sQuery(id+"F10.wireOp",EDGE,"E2.sketch_text.stroke-121"),sQuery(id+"F10.wireOp",EDGE,"E2.sketch_text.stroke-122"),sQuery(id+"F10.wireOp",EDGE,"E2.sketch_text.stroke-123"),sQuery(id+"F10.wireOp",EDGE,"E2.sketch_text.stroke-124"),sQuery(id+"F10.wireOp",EDGE,"E2.sketch_text.stroke-125"),sQuery(id+"F10.wireOp",EDGE,"E2.sketch_text.stroke-126"),sQuery(id+"F10.wireOp",EDGE,"E2.sketch_text.stroke-127"),sQuery(id+"F10.wireOp",EDGE,"E2.sketch_text.stroke-128"),sQuery(id+"F10.wireOp",EDGE,"E2.sketch_text.stroke-129"),sQuery(id+"F10.wireOp",EDGE,"E2.sketch_text.stroke-130"),sQuery(id+"F10.wireOp",EDGE,"E2.sketch_text.stroke-131"),sQuery(id+"F10.wireOp",EDGE,"E2.sketch_text.stroke-132"),sQuery(id+"F10.wireOp",EDGE,"E2.sketch_text.stroke-133"),sQuery(id+"F10.wireOp",EDGE,"E2.sketch_text.stroke-134"),sQuery(id+"F10.wireOp",EDGE,"E2.sketch_text.stroke-135"),sQuery(id+"F10.wireOp",EDGE,"E2.sketch_text.stroke-136"),sQuery(id+"F10.wireOp",EDGE,"E2.sketch_text.stroke-137"),sQuery(id+"F10.wireOp",EDGE,"E2.sketch_text.stroke-138"),sQuery(id+"F10.wireOp",EDGE,"E2.sketch_text.stroke-139"),sQuery(id+"F10.wireOp",EDGE,"E2.sketch_text.stroke-140"),sQuery(id+"F10.wireOp",EDGE,"E2.sketch_text.stroke-141"),sQuery(id+"F10.wireOp",EDGE,"E2.sketch_text.stroke-142"),sQuery(id+"F10.wireOp",EDGE,"E2.sketch_text.stroke-143"),sQuery(id+"F10.wireOp",EDGE,"E2.sketch_text.stroke-144"),sQuery(id+"F10.wireOp",EDGE,"E2.sketch_text.stroke-145"),sQuery(id+"F10.wireOp",EDGE,"E2.sketch_text.stroke-146"),sQuery(id+"F10.wireOp",EDGE,"E2.sketch_text.stroke-147"),sQuery(id+"F10.wireOp",EDGE,"E2.sketch_text.stroke-148"),sQuery(id+"F10.wireOp",EDGE,"E2.sketch_text.stroke-149"),sQuery(id+"F10.wireOp",EDGE,"E2.sketch_text.stroke-150"),sQuery(id+"F10.wireOp",EDGE,"E2.sketch_text.stroke-151"),sQuery(id+"F10.wireOp",EDGE,"E2.sketch_text.stroke-152"),sQuery(id+"F10.wireOp",EDGE,"E2.sketch_text.stroke-153"),sQuery(id+"F10.wireOp",EDGE,"E2.sketch_text.stroke-154"),sQuery(id+"F10.wireOp",EDGE,"E2.sketch_text.stroke-155"),sQuery(id+"F10.wireOp",EDGE,"E2.sketch_text.stroke-156"),sQuery(id+"F10.wireOp",EDGE,"E2.sketch_text.stroke-157"),sQuery(id+"F10.wireOp",EDGE,"E2.sketch_text.stroke-158")])]});
            transform(context, id + "F13", {"entities" : qUnion([Q0]), "transformType" : TransformType.TRANSLATION_3D, "dx" : 0 * mm, "dy" : 0 * mm, "dz" : 1.6 * mm, "makeCopy" : false});
        }
        {
            var Q0;
            Q0=qCreatedBy(makeId("Front.planeOp"),FACE);
            var sketch = newSketch(context, id + "F14", { "sketchPlane" : qUnion([Q0])});
            skLineSegment(sketch, "E3.bottom", {"start": v(46.58, -9.13) * mm, "end": v(109.9, -9.13) * mm});
            skLineSegment(sketch, "E3.top", {"start": v(46.58, -10.02) * mm, "end": v(109.9, -10.02) * mm});
            skLineSegment(sketch, "E3.left", {"start": v(46.58, -9.13) * mm, "end": v(46.58, -10.02) * mm});
            skLineSegment(sketch, "E3.right", {"start": v(109.9, -9.13) * mm, "end": v(109.9, -10.02) * mm});
            skSolve(sketch);
        }
        {
            var Q0;
            Q0 = qSketchRegion(id + "F14", true);
            extrude(context, id + "F15", {"entities" : qUnion([Q0]), "depth" : 3 * mm, "offsetDistance" : 25 * mm});
        }
        {
            var Q0;
            Q0=makeQuery(id+"F11.opExtrude","SWEPT_BODY",BODY,{"disambiguationData":[OSD([sQuery(id+"F10.wireOp",EDGE,"E2.sketch_text.stroke-324"),sQuery(id+"F10.wireOp",EDGE,"E2.sketch_text.stroke-325"),sQuery(id+"F10.wireOp",EDGE,"E2.sketch_text.stroke-326"),sQuery(id+"F10.wireOp",EDGE,"E2.sketch_text.stroke-327"),sQuery(id+"F10.wireOp",EDGE,"E2.sketch_text.stroke-328")])]});
            var Q1;
            Q1=makeQuery(id+"F11.opExtrude","SWEPT_BODY",BODY,{"disambiguationData":[OSD([sQuery(id+"F10.wireOp",EDGE,"E2.sketch_text.stroke-444"),sQuery(id+"F10.wireOp",EDGE,"E2.sketch_text.stroke-445"),sQuery(id+"F10.wireOp",EDGE,"E2.sketch_text.stroke-446"),sQuery(id+"F10.wireOp",EDGE,"E2.sketch_text.stroke-447"),sQuery(id+"F10.wireOp",EDGE,"E2.sketch_text.stroke-448")])]});
            transform(context, id + "F16", {"entities" : qUnion([Q0, Q1]), "transformType" : TransformType.TRANSLATION_3D, "dx" : 0 * mm, "dy" : 0 * mm, "dz" : -0.6 * mm, "makeCopy" : false});
        }
        {
            var Q0;
            Q0=makeQuery(id+"F11.opExtrude","SWEPT_BODY",BODY,{"disambiguationData":[OSD([sQuery(id+"F10.wireOp",EDGE,"E2.sketch_text.stroke-19"),sQuery(id+"F10.wireOp",EDGE,"E2.sketch_text.stroke-20"),sQuery(id+"F10.wireOp",EDGE,"E2.sketch_text.stroke-21"),sQuery(id+"F10.wireOp",EDGE,"E2.sketch_text.stroke-22"),sQuery(id+"F10.wireOp",EDGE,"E2.sketch_text.stroke-23"),sQuery(id+"F10.wireOp",EDGE,"E2.sketch_text.stroke-24"),sQuery(id+"F10.wireOp",EDGE,"E2.sketch_text.stroke-25"),sQuery(id+"F10.wireOp",EDGE,"E2.sketch_text.stroke-26"),sQuery(id+"F10.wireOp",EDGE,"E2.sketch_text.stroke-27"),sQuery(id+"F10.wireOp",EDGE,"E2.sketch_text.stroke-28"),sQuery(id+"F10.wireOp",EDGE,"E2.sketch_text.stroke-29"),sQuery(id+"F10.wireOp",EDGE,"E2.sketch_text.stroke-30"),sQuery(id+"F10.wireOp",EDGE,"E2.sketch_text.stroke-31"),sQuery(id+"F10.wireOp",EDGE,"E2.sketch_text.stroke-32"),sQuery(id+"F10.wireOp",EDGE,"E2.sketch_text.stroke-33"),sQuery(id+"F10.wireOp",EDGE,"E2.sketch_text.stroke-34"),sQuery(id+"F10.wireOp",EDGE,"E2.sketch_text.stroke-35"),sQuery(id+"F10.wireOp",EDGE,"E2.sketch_text.stroke-36"),sQuery(id+"F10.wireOp",EDGE,"E2.sketch_text.stroke-37"),sQuery(id+"F10.wireOp",EDGE,"E2.sketch_text.stroke-38"),sQuery(id+"F10.wireOp",EDGE,"E2.sketch_text.stroke-39"),sQuery(id+"F10.wireOp",EDGE,"E2.sketch_text.stroke-40"),sQuery(id+"F10.wireOp",EDGE,"E2.sketch_text.stroke-41"),sQuery(id+"F10.wireOp",EDGE,"E2.sketch_text.stroke-42"),sQuery(id+"F10.wireOp",EDGE,"E2.sketch_text.stroke-43")])]});
            transform(context, id + "F17", {"entities" : qUnion([Q0]), "transformType" : TransformType.TRANSLATION_3D, "dx" : 0 * mm, "dy" : 0 * mm, "dz" : -.4 * mm, "makeCopy" : false});
        }
        {
            var Q0;
            Q0=makeQuery(id+"F11.opExtrude","SWEPT_BODY",BODY,{"disambiguationData":[OSD([sQuery(id+"F10.wireOp",EDGE,"E2.sketch_text.stroke-275"),sQuery(id+"F10.wireOp",EDGE,"E2.sketch_text.stroke-276"),sQuery(id+"F10.wireOp",EDGE,"E2.sketch_text.stroke-277"),sQuery(id+"F10.wireOp",EDGE,"E2.sketch_text.stroke-278"),sQuery(id+"F10.wireOp",EDGE,"E2.sketch_text.stroke-279"),sQuery(id+"F10.wireOp",EDGE,"E2.sketch_text.stroke-280"),sQuery(id+"F10.wireOp",EDGE,"E2.sketch_text.stroke-281"),sQuery(id+"F10.wireOp",EDGE,"E2.sketch_text.stroke-282"),sQuery(id+"F10.wireOp",EDGE,"E2.sketch_text.stroke-283"),sQuery(id+"F10.wireOp",EDGE,"E2.sketch_text.stroke-284"),sQuery(id+"F10.wireOp",EDGE,"E2.sketch_text.stroke-285"),sQuery(id+"F10.wireOp",EDGE,"E2.sketch_text.stroke-286"),sQuery(id+"F10.wireOp",EDGE,"E2.sketch_text.stroke-287"),sQuery(id+"F10.wireOp",EDGE,"E2.sketch_text.stroke-288")])]});
            var Q1;
            Q1=makeQuery(id+"F11.opExtrude","SWEPT_BODY",BODY,{"disambiguationData":[OSD([sQuery(id+"F10.wireOp",EDGE,"E2.sketch_text.stroke-307"),sQuery(id+"F10.wireOp",EDGE,"E2.sketch_text.stroke-308"),sQuery(id+"F10.wireOp",EDGE,"E2.sketch_text.stroke-309"),sQuery(id+"F10.wireOp",EDGE,"E2.sketch_text.stroke-310")])]});
            var Q2;
            Q2=makeQuery(id+"F11.opExtrude","SWEPT_BODY",BODY,{"disambiguationData":[OSD([sQuery(id+"F10.wireOp",EDGE,"E2.sketch_text.stroke-376"),sQuery(id+"F10.wireOp",EDGE,"E2.sketch_text.stroke-377"),sQuery(id+"F10.wireOp",EDGE,"E2.sketch_text.stroke-378"),sQuery(id+"F10.wireOp",EDGE,"E2.sketch_text.stroke-379"),sQuery(id+"F10.wireOp",EDGE,"E2.sketch_text.stroke-380"),sQuery(id+"F10.wireOp",EDGE,"E2.sketch_text.stroke-381"),sQuery(id+"F10.wireOp",EDGE,"E2.sketch_text.stroke-382"),sQuery(id+"F10.wireOp",EDGE,"E2.sketch_text.stroke-383"),sQuery(id+"F10.wireOp",EDGE,"E2.sketch_text.stroke-384"),sQuery(id+"F10.wireOp",EDGE,"E2.sketch_text.stroke-385"),sQuery(id+"F10.wireOp",EDGE,"E2.sketch_text.stroke-386"),sQuery(id+"F10.wireOp",EDGE,"E2.sketch_text.stroke-387")])]});
            var Q3;
            Q3=makeQuery(id+"F11.opExtrude","SWEPT_BODY",BODY,{"disambiguationData":[OSD([sQuery(id+"F10.wireOp",EDGE,"E2.sketch_text.stroke-333"),sQuery(id+"F10.wireOp",EDGE,"E2.sketch_text.stroke-334"),sQuery(id+"F10.wireOp",EDGE,"E2.sketch_text.stroke-335"),sQuery(id+"F10.wireOp",EDGE,"E2.sketch_text.stroke-336"),sQuery(id+"F10.wireOp",EDGE,"E2.sketch_text.stroke-337"),sQuery(id+"F10.wireOp",EDGE,"E2.sketch_text.stroke-338"),sQuery(id+"F10.wireOp",EDGE,"E2.sketch_text.stroke-339"),sQuery(id+"F10.wireOp",EDGE,"E2.sketch_text.stroke-340"),sQuery(id+"F10.wireOp",EDGE,"E2.sketch_text.stroke-341"),sQuery(id+"F10.wireOp",EDGE,"E2.sketch_text.stroke-342"),sQuery(id+"F10.wireOp",EDGE,"E2.sketch_text.stroke-343"),sQuery(id+"F10.wireOp",EDGE,"E2.sketch_text.stroke-344"),sQuery(id+"F10.wireOp",EDGE,"E2.sketch_text.stroke-345"),sQuery(id+"F10.wireOp",EDGE,"E2.sketch_text.stroke-346"),sQuery(id+"F10.wireOp",EDGE,"E2.sketch_text.stroke-347"),sQuery(id+"F10.wireOp",EDGE,"E2.sketch_text.stroke-348"),sQuery(id+"F10.wireOp",EDGE,"E2.sketch_text.stroke-349"),sQuery(id+"F10.wireOp",EDGE,"E2.sketch_text.stroke-350"),sQuery(id+"F10.wireOp",EDGE,"E2.sketch_text.stroke-351"),sQuery(id+"F10.wireOp",EDGE,"E2.sketch_text.stroke-352"),sQuery(id+"F10.wireOp",EDGE,"E2.sketch_text.stroke-353"),sQuery(id+"F10.wireOp",EDGE,"E2.sketch_text.stroke-354"),sQuery(id+"F10.wireOp",EDGE,"E2.sketch_text.stroke-355"),sQuery(id+"F10.wireOp",EDGE,"E2.sketch_text.stroke-356"),sQuery(id+"F10.wireOp",EDGE,"E2.sketch_text.stroke-357"),sQuery(id+"F10.wireOp",EDGE,"E2.sketch_text.stroke-358")])]});
            var Q4;
            Q4=makeQuery(id+"F11.opExtrude","SWEPT_BODY",BODY,{"disambiguationData":[OSD([sQuery(id+"F10.wireOp",EDGE,"E2.sketch_text.stroke-329"),sQuery(id+"F10.wireOp",EDGE,"E2.sketch_text.stroke-330"),sQuery(id+"F10.wireOp",EDGE,"E2.sketch_text.stroke-331"),sQuery(id+"F10.wireOp",EDGE,"E2.sketch_text.stroke-332")])]});
            var Q5;
            Q5=makeQuery(id+"F11.opExtrude","SWEPT_BODY",BODY,{"disambiguationData":[OSD([sQuery(id+"F10.wireOp",EDGE,"E2.sketch_text.stroke-324"),sQuery(id+"F10.wireOp",EDGE,"E2.sketch_text.stroke-325"),sQuery(id+"F10.wireOp",EDGE,"E2.sketch_text.stroke-326"),sQuery(id+"F10.wireOp",EDGE,"E2.sketch_text.stroke-327"),sQuery(id+"F10.wireOp",EDGE,"E2.sketch_text.stroke-328")])]});
            var Q6;
            Q6=makeQuery(id+"F11.opExtrude","SWEPT_BODY",BODY,{"disambiguationData":[OSD([sQuery(id+"F10.wireOp",EDGE,"E2.sketch_text.stroke-311"),sQuery(id+"F10.wireOp",EDGE,"E2.sketch_text.stroke-312"),sQuery(id+"F10.wireOp",EDGE,"E2.sketch_text.stroke-313"),sQuery(id+"F10.wireOp",EDGE,"E2.sketch_text.stroke-314"),sQuery(id+"F10.wireOp",EDGE,"E2.sketch_text.stroke-315"),sQuery(id+"F10.wireOp",EDGE,"E2.sketch_text.stroke-316"),sQuery(id+"F10.wireOp",EDGE,"E2.sketch_text.stroke-317"),sQuery(id+"F10.wireOp",EDGE,"E2.sketch_text.stroke-318"),sQuery(id+"F10.wireOp",EDGE,"E2.sketch_text.stroke-319"),sQuery(id+"F10.wireOp",EDGE,"E2.sketch_text.stroke-320"),sQuery(id+"F10.wireOp",EDGE,"E2.sketch_text.stroke-321"),sQuery(id+"F10.wireOp",EDGE,"E2.sketch_text.stroke-322"),sQuery(id+"F10.wireOp",EDGE,"E2.sketch_text.stroke-323")])]});
            var Q7;
            Q7=makeQuery(id+"F11.opExtrude","SWEPT_BODY",BODY,{"disambiguationData":[OSD([sQuery(id+"F10.wireOp",EDGE,"E2.sketch_text.stroke-388"),sQuery(id+"F10.wireOp",EDGE,"E2.sketch_text.stroke-389"),sQuery(id+"F10.wireOp",EDGE,"E2.sketch_text.stroke-390"),sQuery(id+"F10.wireOp",EDGE,"E2.sketch_text.stroke-391"),sQuery(id+"F10.wireOp",EDGE,"E2.sketch_text.stroke-392"),sQuery(id+"F10.wireOp",EDGE,"E2.sketch_text.stroke-393"),sQuery(id+"F10.wireOp",EDGE,"E2.sketch_text.stroke-394"),sQuery(id+"F10.wireOp",EDGE,"E2.sketch_text.stroke-395"),sQuery(id+"F10.wireOp",EDGE,"E2.sketch_text.stroke-396"),sQuery(id+"F10.wireOp",EDGE,"E2.sketch_text.stroke-397"),sQuery(id+"F10.wireOp",EDGE,"E2.sketch_text.stroke-398"),sQuery(id+"F10.wireOp",EDGE,"E2.sketch_text.stroke-399"),sQuery(id+"F10.wireOp",EDGE,"E2.sketch_text.stroke-400"),sQuery(id+"F10.wireOp",EDGE,"E2.sketch_text.stroke-401"),sQuery(id+"F10.wireOp",EDGE,"E2.sketch_text.stroke-402"),sQuery(id+"F10.wireOp",EDGE,"E2.sketch_text.stroke-403"),sQuery(id+"F10.wireOp",EDGE,"E2.sketch_text.stroke-404"),sQuery(id+"F10.wireOp",EDGE,"E2.sketch_text.stroke-405"),sQuery(id+"F10.wireOp",EDGE,"E2.sketch_text.stroke-406"),sQuery(id+"F10.wireOp",EDGE,"E2.sketch_text.stroke-407"),sQuery(id+"F10.wireOp",EDGE,"E2.sketch_text.stroke-408"),sQuery(id+"F10.wireOp",EDGE,"E2.sketch_text.stroke-409"),sQuery(id+"F10.wireOp",EDGE,"E2.sketch_text.stroke-410"),sQuery(id+"F10.wireOp",EDGE,"E2.sketch_text.stroke-411"),sQuery(id+"F10.wireOp",EDGE,"E2.sketch_text.stroke-412")])]});
            var Q8;
            Q8=makeQuery(id+"F11.opExtrude","SWEPT_BODY",BODY,{"disambiguationData":[OSD([sQuery(id+"F10.wireOp",EDGE,"E2.sketch_text.stroke-413"),sQuery(id+"F10.wireOp",EDGE,"E2.sketch_text.stroke-414"),sQuery(id+"F10.wireOp",EDGE,"E2.sketch_text.stroke-415"),sQuery(id+"F10.wireOp",EDGE,"E2.sketch_text.stroke-416"),sQuery(id+"F10.wireOp",EDGE,"E2.sketch_text.stroke-417"),sQuery(id+"F10.wireOp",EDGE,"E2.sketch_text.stroke-418"),sQuery(id+"F10.wireOp",EDGE,"E2.sketch_text.stroke-419"),sQuery(id+"F10.wireOp",EDGE,"E2.sketch_text.stroke-420"),sQuery(id+"F10.wireOp",EDGE,"E2.sketch_text.stroke-421"),sQuery(id+"F10.wireOp",EDGE,"E2.sketch_text.stroke-422"),sQuery(id+"F10.wireOp",EDGE,"E2.sketch_text.stroke-423"),sQuery(id+"F10.wireOp",EDGE,"E2.sketch_text.stroke-424"),sQuery(id+"F10.wireOp",EDGE,"E2.sketch_text.stroke-425"),sQuery(id+"F10.wireOp",EDGE,"E2.sketch_text.stroke-426"),sQuery(id+"F10.wireOp",EDGE,"E2.sketch_text.stroke-427"),sQuery(id+"F10.wireOp",EDGE,"E2.sketch_text.stroke-428"),sQuery(id+"F10.wireOp",EDGE,"E2.sketch_text.stroke-429")])]});
            var Q9;
            Q9=makeQuery(id+"F11.opExtrude","SWEPT_BODY",BODY,{"disambiguationData":[OSD([sQuery(id+"F10.wireOp",EDGE,"E2.sketch_text.stroke-430"),sQuery(id+"F10.wireOp",EDGE,"E2.sketch_text.stroke-431"),sQuery(id+"F10.wireOp",EDGE,"E2.sketch_text.stroke-432"),sQuery(id+"F10.wireOp",EDGE,"E2.sketch_text.stroke-433"),sQuery(id+"F10.wireOp",EDGE,"E2.sketch_text.stroke-434"),sQuery(id+"F10.wireOp",EDGE,"E2.sketch_text.stroke-435"),sQuery(id+"F10.wireOp",EDGE,"E2.sketch_text.stroke-436"),sQuery(id+"F10.wireOp",EDGE,"E2.sketch_text.stroke-437"),sQuery(id+"F10.wireOp",EDGE,"E2.sketch_text.stroke-438"),sQuery(id+"F10.wireOp",EDGE,"E2.sketch_text.stroke-439"),sQuery(id+"F10.wireOp",EDGE,"E2.sketch_text.stroke-440"),sQuery(id+"F10.wireOp",EDGE,"E2.sketch_text.stroke-441"),sQuery(id+"F10.wireOp",EDGE,"E2.sketch_text.stroke-442"),sQuery(id+"F10.wireOp",EDGE,"E2.sketch_text.stroke-443")])]});
            var Q10;
            Q10=makeQuery(id+"F11.opExtrude","SWEPT_BODY",BODY,{"disambiguationData":[OSD([sQuery(id+"F10.wireOp",EDGE,"E2.sketch_text.stroke-444"),sQuery(id+"F10.wireOp",EDGE,"E2.sketch_text.stroke-445"),sQuery(id+"F10.wireOp",EDGE,"E2.sketch_text.stroke-446"),sQuery(id+"F10.wireOp",EDGE,"E2.sketch_text.stroke-447"),sQuery(id+"F10.wireOp",EDGE,"E2.sketch_text.stroke-448")])]});
            var Q11;
            Q11=makeQuery(id+"F11.opExtrude","SWEPT_BODY",BODY,{"disambiguationData":[OSD([sQuery(id+"F10.wireOp",EDGE,"E2.sketch_text.stroke-449"),sQuery(id+"F10.wireOp",EDGE,"E2.sketch_text.stroke-450"),sQuery(id+"F10.wireOp",EDGE,"E2.sketch_text.stroke-451"),sQuery(id+"F10.wireOp",EDGE,"E2.sketch_text.stroke-452")])]});
            var Q12;
            Q12=makeQuery(id+"F11.opExtrude","SWEPT_BODY",BODY,{"disambiguationData":[OSD([sQuery(id+"F10.wireOp",EDGE,"E2.sketch_text.stroke-453"),sQuery(id+"F10.wireOp",EDGE,"E2.sketch_text.stroke-454"),sQuery(id+"F10.wireOp",EDGE,"E2.sketch_text.stroke-455"),sQuery(id+"F10.wireOp",EDGE,"E2.sketch_text.stroke-456"),sQuery(id+"F10.wireOp",EDGE,"E2.sketch_text.stroke-457"),sQuery(id+"F10.wireOp",EDGE,"E2.sketch_text.stroke-458"),sQuery(id+"F10.wireOp",EDGE,"E2.sketch_text.stroke-459"),sQuery(id+"F10.wireOp",EDGE,"E2.sketch_text.stroke-460"),sQuery(id+"F10.wireOp",EDGE,"E2.sketch_text.stroke-461"),sQuery(id+"F10.wireOp",EDGE,"E2.sketch_text.stroke-462"),sQuery(id+"F10.wireOp",EDGE,"E2.sketch_text.stroke-463"),sQuery(id+"F10.wireOp",EDGE,"E2.sketch_text.stroke-464"),sQuery(id+"F10.wireOp",EDGE,"E2.sketch_text.stroke-465"),sQuery(id+"F10.wireOp",EDGE,"E2.sketch_text.stroke-466"),sQuery(id+"F10.wireOp",EDGE,"E2.sketch_text.stroke-467"),sQuery(id+"F10.wireOp",EDGE,"E2.sketch_text.stroke-468"),sQuery(id+"F10.wireOp",EDGE,"E2.sketch_text.stroke-469")])]});
            var Q13;
            Q13=makeQuery(id+"F11.opExtrude","SWEPT_BODY",BODY,{"disambiguationData":[OSD([sQuery(id+"F10.wireOp",EDGE,"E2.sketch_text.stroke-470"),sQuery(id+"F10.wireOp",EDGE,"E2.sketch_text.stroke-471"),sQuery(id+"F10.wireOp",EDGE,"E2.sketch_text.stroke-472"),sQuery(id+"F10.wireOp",EDGE,"E2.sketch_text.stroke-473"),sQuery(id+"F10.wireOp",EDGE,"E2.sketch_text.stroke-474"),sQuery(id+"F10.wireOp",EDGE,"E2.sketch_text.stroke-475"),sQuery(id+"F10.wireOp",EDGE,"E2.sketch_text.stroke-476"),sQuery(id+"F10.wireOp",EDGE,"E2.sketch_text.stroke-477"),sQuery(id+"F10.wireOp",EDGE,"E2.sketch_text.stroke-478"),sQuery(id+"F10.wireOp",EDGE,"E2.sketch_text.stroke-479"),sQuery(id+"F10.wireOp",EDGE,"E2.sketch_text.stroke-480"),sQuery(id+"F10.wireOp",EDGE,"E2.sketch_text.stroke-481"),sQuery(id+"F10.wireOp",EDGE,"E2.sketch_text.stroke-482"),sQuery(id+"F10.wireOp",EDGE,"E2.sketch_text.stroke-483"),sQuery(id+"F10.wireOp",EDGE,"E2.sketch_text.stroke-484"),sQuery(id+"F10.wireOp",EDGE,"E2.sketch_text.stroke-485"),sQuery(id+"F10.wireOp",EDGE,"E2.sketch_text.stroke-486"),sQuery(id+"F10.wireOp",EDGE,"E2.sketch_text.stroke-487"),sQuery(id+"F10.wireOp",EDGE,"E2.sketch_text.stroke-488"),sQuery(id+"F10.wireOp",EDGE,"E2.sketch_text.stroke-489"),sQuery(id+"F10.wireOp",EDGE,"E2.sketch_text.stroke-490"),sQuery(id+"F10.wireOp",EDGE,"E2.sketch_text.stroke-491"),sQuery(id+"F10.wireOp",EDGE,"E2.sketch_text.stroke-492"),sQuery(id+"F10.wireOp",EDGE,"E2.sketch_text.stroke-493"),sQuery(id+"F10.wireOp",EDGE,"E2.sketch_text.stroke-494"),sQuery(id+"F10.wireOp",EDGE,"E2.sketch_text.stroke-495"),sQuery(id+"F10.wireOp",EDGE,"E2.sketch_text.stroke-496"),sQuery(id+"F10.wireOp",EDGE,"E2.sketch_text.stroke-497"),sQuery(id+"F10.wireOp",EDGE,"E2.sketch_text.stroke-498"),sQuery(id+"F10.wireOp",EDGE,"E2.sketch_text.stroke-499"),sQuery(id+"F10.wireOp",EDGE,"E2.sketch_text.stroke-500"),sQuery(id+"F10.wireOp",EDGE,"E2.sketch_text.stroke-501"),sQuery(id+"F10.wireOp",EDGE,"E2.sketch_text.stroke-502"),sQuery(id+"F10.wireOp",EDGE,"E2.sketch_text.stroke-503"),sQuery(id+"F10.wireOp",EDGE,"E2.sketch_text.stroke-504"),sQuery(id+"F10.wireOp",EDGE,"E2.sketch_text.stroke-505"),sQuery(id+"F10.wireOp",EDGE,"E2.sketch_text.stroke-506"),sQuery(id+"F10.wireOp",EDGE,"E2.sketch_text.stroke-507"),sQuery(id+"F10.wireOp",EDGE,"E2.sketch_text.stroke-508"),sQuery(id+"F10.wireOp",EDGE,"E2.sketch_text.stroke-509"),sQuery(id+"F10.wireOp",EDGE,"E2.sketch_text.stroke-510"),sQuery(id+"F10.wireOp",EDGE,"E2.sketch_text.stroke-511"),sQuery(id+"F10.wireOp",EDGE,"E2.sketch_text.stroke-512"),sQuery(id+"F10.wireOp",EDGE,"E2.sketch_text.stroke-513")])]});
            transform(context, id + "F18", {"entities" : qUnion([Q0, Q1, Q2, Q3, Q4, Q5, Q6, Q7, Q8, Q9, Q10, Q11, Q12, Q13]), "transformType" : TransformType.TRANSLATION_3D, "dx" : 0 * mm, "dy" : 0 * mm, "dz" : .3 * mm, "makeCopy" : false});
        }
        {
            var Q0;
            Q0=makeQuery(id+"F11.opExtrude","SWEPT_BODY",BODY,{"disambiguationData":[OSD([sQuery(id+"F10.wireOp",EDGE,"E2.sketch_text.stroke-470"),sQuery(id+"F10.wireOp",EDGE,"E2.sketch_text.stroke-471"),sQuery(id+"F10.wireOp",EDGE,"E2.sketch_text.stroke-472"),sQuery(id+"F10.wireOp",EDGE,"E2.sketch_text.stroke-473"),sQuery(id+"F10.wireOp",EDGE,"E2.sketch_text.stroke-474"),sQuery(id+"F10.wireOp",EDGE,"E2.sketch_text.stroke-475"),sQuery(id+"F10.wireOp",EDGE,"E2.sketch_text.stroke-476"),sQuery(id+"F10.wireOp",EDGE,"E2.sketch_text.stroke-477"),sQuery(id+"F10.wireOp",EDGE,"E2.sketch_text.stroke-478"),sQuery(id+"F10.wireOp",EDGE,"E2.sketch_text.stroke-479"),sQuery(id+"F10.wireOp",EDGE,"E2.sketch_text.stroke-480"),sQuery(id+"F10.wireOp",EDGE,"E2.sketch_text.stroke-481"),sQuery(id+"F10.wireOp",EDGE,"E2.sketch_text.stroke-482"),sQuery(id+"F10.wireOp",EDGE,"E2.sketch_text.stroke-483"),sQuery(id+"F10.wireOp",EDGE,"E2.sketch_text.stroke-484"),sQuery(id+"F10.wireOp",EDGE,"E2.sketch_text.stroke-485"),sQuery(id+"F10.wireOp",EDGE,"E2.sketch_text.stroke-486"),sQuery(id+"F10.wireOp",EDGE,"E2.sketch_text.stroke-487"),sQuery(id+"F10.wireOp",EDGE,"E2.sketch_text.stroke-488"),sQuery(id+"F10.wireOp",EDGE,"E2.sketch_text.stroke-489"),sQuery(id+"F10.wireOp",EDGE,"E2.sketch_text.stroke-490"),sQuery(id+"F10.wireOp",EDGE,"E2.sketch_text.stroke-491"),sQuery(id+"F10.wireOp",EDGE,"E2.sketch_text.stroke-492"),sQuery(id+"F10.wireOp",EDGE,"E2.sketch_text.stroke-493"),sQuery(id+"F10.wireOp",EDGE,"E2.sketch_text.stroke-494"),sQuery(id+"F10.wireOp",EDGE,"E2.sketch_text.stroke-495"),sQuery(id+"F10.wireOp",EDGE,"E2.sketch_text.stroke-496"),sQuery(id+"F10.wireOp",EDGE,"E2.sketch_text.stroke-497"),sQuery(id+"F10.wireOp",EDGE,"E2.sketch_text.stroke-498"),sQuery(id+"F10.wireOp",EDGE,"E2.sketch_text.stroke-499"),sQuery(id+"F10.wireOp",EDGE,"E2.sketch_text.stroke-500"),sQuery(id+"F10.wireOp",EDGE,"E2.sketch_text.stroke-501"),sQuery(id+"F10.wireOp",EDGE,"E2.sketch_text.stroke-502"),sQuery(id+"F10.wireOp",EDGE,"E2.sketch_text.stroke-503"),sQuery(id+"F10.wireOp",EDGE,"E2.sketch_text.stroke-504"),sQuery(id+"F10.wireOp",EDGE,"E2.sketch_text.stroke-505"),sQuery(id+"F10.wireOp",EDGE,"E2.sketch_text.stroke-506"),sQuery(id+"F10.wireOp",EDGE,"E2.sketch_text.stroke-507"),sQuery(id+"F10.wireOp",EDGE,"E2.sketch_text.stroke-508"),sQuery(id+"F10.wireOp",EDGE,"E2.sketch_text.stroke-509"),sQuery(id+"F10.wireOp",EDGE,"E2.sketch_text.stroke-510"),sQuery(id+"F10.wireOp",EDGE,"E2.sketch_text.stroke-511"),sQuery(id+"F10.wireOp",EDGE,"E2.sketch_text.stroke-512"),sQuery(id+"F10.wireOp",EDGE,"E2.sketch_text.stroke-513")])]});
            transform(context, id + "F19", {"entities" : qUnion([Q0]), "transformType" : TransformType.TRANSLATION_3D, "dx" : 0 * mm, "dy" : 0 * mm, "dz" : 1.5 * mm, "makeCopy" : false});
        }
        {
            var Q0;
            Q0=qCreatedBy(makeId("Front.planeOp"),FACE);
            var sketch = newSketch(context, id + "F20", { "sketchPlane" : qUnion([Q0])});
            skLineSegment(sketch, "E4.bottom", {"start": v(46.97, -15.74) * mm, "end": v(110.44, -15.74) * mm});
            skLineSegment(sketch, "E4.top", {"start": v(46.97, -17) * mm, "end": v(110.44, -17) * mm});
            skLineSegment(sketch, "E4.left", {"start": v(46.97, -15.74) * mm, "end": v(46.97, -17) * mm});
            skLineSegment(sketch, "E4.right", {"start": v(110.44, -15.74) * mm, "end": v(110.44, -17) * mm});
            skSolve(sketch);
        }
        {
            var Q0;
            Q0 = qSketchRegion(id + "F20", true);
            extrude(context, id + "F21", {"entities" : qUnion([Q0]), "depth" : 4 * mm, "offsetDistance" : 25 * mm});
        }
        {
            var Q0;
            Q0=qCreatedBy(makeId("Front.planeOp"),FACE);
            var sketch = newSketch(context, id + "F22", { "sketchPlane" : qUnion([Q0])});
            skText(sketch, "E5", { "text": "Bray Emmets", "fontName": "OpenSans-Bold.ttf"});
            const initialGuessF22  = {"E5": [-0.02462, -0.04836, 1, 0, 0.0076]};
            skSetInitialGuess(sketch, initialGuessF22);
            skSolve(sketch);
        }
        {
            var Q0;
            Q0 = qSketchRegion(id + "F22", true);
            extrude(context, id + "F23", {"entities" : qUnion([Q0]), "depth" : 3.5 * mm, "offsetDistance" : 25 * mm});
        }
        {
            var Q0;
            Q0=makeQuery(id+"F23.opExtrude","SWEPT_BODY",BODY,{"disambiguationData":[OSD([sQuery(id+"F22.wireOp",EDGE,"E5.sketch_text.stroke-63"),sQuery(id+"F22.wireOp",EDGE,"E5.sketch_text.stroke-64"),sQuery(id+"F22.wireOp",EDGE,"E5.sketch_text.stroke-65"),sQuery(id+"F22.wireOp",EDGE,"E5.sketch_text.stroke-66"),sQuery(id+"F22.wireOp",EDGE,"E5.sketch_text.stroke-67"),sQuery(id+"F22.wireOp",EDGE,"E5.sketch_text.stroke-68"),sQuery(id+"F22.wireOp",EDGE,"E5.sketch_text.stroke-69"),sQuery(id+"F22.wireOp",EDGE,"E5.sketch_text.stroke-70"),sQuery(id+"F22.wireOp",EDGE,"E5.sketch_text.stroke-71"),sQuery(id+"F22.wireOp",EDGE,"E5.sketch_text.stroke-72"),sQuery(id+"F22.wireOp",EDGE,"E5.sketch_text.stroke-73"),sQuery(id+"F22.wireOp",EDGE,"E5.sketch_text.stroke-74"),sQuery(id+"F22.wireOp",EDGE,"E5.sketch_text.stroke-75"),sQuery(id+"F22.wireOp",EDGE,"E5.sketch_text.stroke-76"),sQuery(id+"F22.wireOp",EDGE,"E5.sketch_text.stroke-77"),sQuery(id+"F22.wireOp",EDGE,"E5.sketch_text.stroke-78"),sQuery(id+"F22.wireOp",EDGE,"E5.sketch_text.stroke-79")])]});
            transform(context, id + "F24", {"entities" : qUnion([Q0]), "transformType" : TransformType.TRANSLATION_3D, "dx" : 0 * mm, "dy" : 0 * mm, "dz" : 2.4 * mm, "makeCopy" : false});
        }
        {
            var Q0;
            Q0=qCreatedBy(makeId("Front.planeOp"),FACE);
            var sketch = newSketch(context, id + "F25", { "sketchPlane" : qUnion([Q0])});
            skLineSegment(sketch, "E6.bottom", {"start": v(-25.02, -48.3) * mm, "end": v(45.4, -48.3) * mm});
            skLineSegment(sketch, "E6.top", {"start": v(-25.02, -49.37) * mm, "end": v(45.4, -49.37) * mm});
            skLineSegment(sketch, "E6.left", {"start": v(-25.02, -48.3) * mm, "end": v(-25.02, -49.37) * mm});
            skLineSegment(sketch, "E6.right", {"start": v(45.4, -48.3) * mm, "end": v(45.4, -49.37) * mm});
            skSolve(sketch);
        }
        {
            var Q0;
            Q0 = qSketchRegion(id + "F25", true);
            extrude(context, id + "F26", {"entities" : qUnion([Q0]), "depth" : 4 * mm, "offsetDistance" : 25 * mm});
        }
        {
            var Q0;
            Q0=makeQuery(id+"F11.opExtrude","SWEPT_BODY",BODY,{"disambiguationData":[OSD([sQuery(id+"F10.wireOp",EDGE,"E2.sketch_text.stroke-19"),sQuery(id+"F10.wireOp",EDGE,"E2.sketch_text.stroke-20"),sQuery(id+"F10.wireOp",EDGE,"E2.sketch_text.stroke-21"),sQuery(id+"F10.wireOp",EDGE,"E2.sketch_text.stroke-22"),sQuery(id+"F10.wireOp",EDGE,"E2.sketch_text.stroke-23"),sQuery(id+"F10.wireOp",EDGE,"E2.sketch_text.stroke-24"),sQuery(id+"F10.wireOp",EDGE,"E2.sketch_text.stroke-25"),sQuery(id+"F10.wireOp",EDGE,"E2.sketch_text.stroke-26"),sQuery(id+"F10.wireOp",EDGE,"E2.sketch_text.stroke-27"),sQuery(id+"F10.wireOp",EDGE,"E2.sketch_text.stroke-28"),sQuery(id+"F10.wireOp",EDGE,"E2.sketch_text.stroke-29"),sQuery(id+"F10.wireOp",EDGE,"E2.sketch_text.stroke-30"),sQuery(id+"F10.wireOp",EDGE,"E2.sketch_text.stroke-31"),sQuery(id+"F10.wireOp",EDGE,"E2.sketch_text.stroke-32"),sQuery(id+"F10.wireOp",EDGE,"E2.sketch_text.stroke-33"),sQuery(id+"F10.wireOp",EDGE,"E2.sketch_text.stroke-34"),sQuery(id+"F10.wireOp",EDGE,"E2.sketch_text.stroke-35"),sQuery(id+"F10.wireOp",EDGE,"E2.sketch_text.stroke-36"),sQuery(id+"F10.wireOp",EDGE,"E2.sketch_text.stroke-37"),sQuery(id+"F10.wireOp",EDGE,"E2.sketch_text.stroke-38"),sQuery(id+"F10.wireOp",EDGE,"E2.sketch_text.stroke-39"),sQuery(id+"F10.wireOp",EDGE,"E2.sketch_text.stroke-40"),sQuery(id+"F10.wireOp",EDGE,"E2.sketch_text.stroke-41"),sQuery(id+"F10.wireOp",EDGE,"E2.sketch_text.stroke-42"),sQuery(id+"F10.wireOp",EDGE,"E2.sketch_text.stroke-43")])]});
            var Q1;
            Q1=makeQuery(id+"F21.opExtrude","CAP_VERTEX",VERTEX,{"disambiguationData":[OSD([sQuery(id+"F20.wireOp",EDGE,"E4.top"),sQuery(id+"F20.wireOp",EDGE,"E4.left")])],"isStart":true});
            transform(context, id + "F27", {"entities" : qUnion([Q0]), "transformType" : TransformType.SCALE_UNIFORMLY, "scale" : .75, "scalePoint" : qUnion([Q1]), "makeCopy" : false});
        }
    });